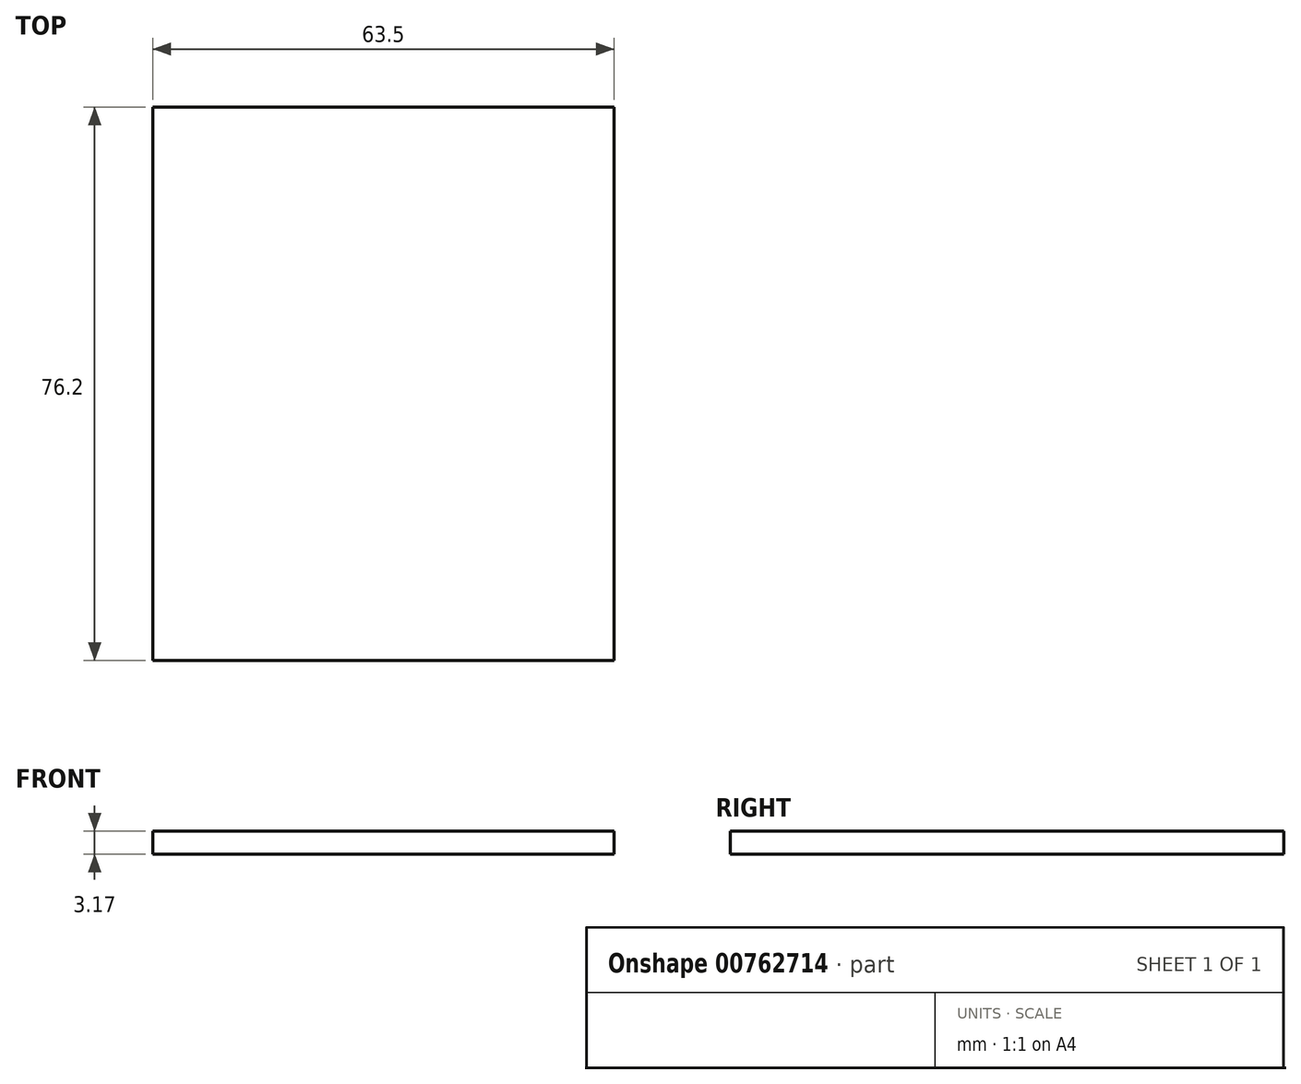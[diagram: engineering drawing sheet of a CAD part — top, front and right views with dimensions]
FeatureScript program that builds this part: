
annotation { "Feature Type Name" : "Feature", "Feature Type Description" : "" }
export const myFeature = defineFeature(function(context is Context, id is Id, definition is map)
    precondition{}
    {
        {
            var Q0;
            Q0=qCreatedBy(makeId("Top.planeOp"),FACE);
            var sketch = newSketch(context, id + "F0", { "sketchPlane" : qUnion([Q0])});
            skLineSegment(sketch, "E0", {"start": v(0, 33) * mm, "end": v(31.75, 33) * mm});
            skLineSegment(sketch, "E1", {"start": v(0, 33) * mm, "end": v(-31.75, 33) * mm});
            skLineSegment(sketch, "E2", {"start": v(-31.75, 33) * mm, "end": v(-31.75, -43.2) * mm});
            skLineSegment(sketch, "E3", {"start": v(31.75, 33) * mm, "end": v(31.75, -43.2) * mm});
            skLineSegment(sketch, "E4", {"start": v(-31.75, -43.2) * mm, "end": v(31.75, -43.2) * mm});
            skSolve(sketch);
        }
        {
            var Q0;
            Q0=makeQuery(id+"F0.imprint","IMPRINT",FACE,{"disambiguationData":[TD([[makeQuery(id+"F0.imprint","IMPRINT",EDGE,{"derivedFrom":sQuery(id+"F0.wireOp",EDGE,"E0")}),-1.0]])]});
            extrude(context, id + "F1", {"entities" : qUnion([Q0]), "depth" : 3.17 * mm, "offsetDistance" : 25.4 * mm});
        }
    });
